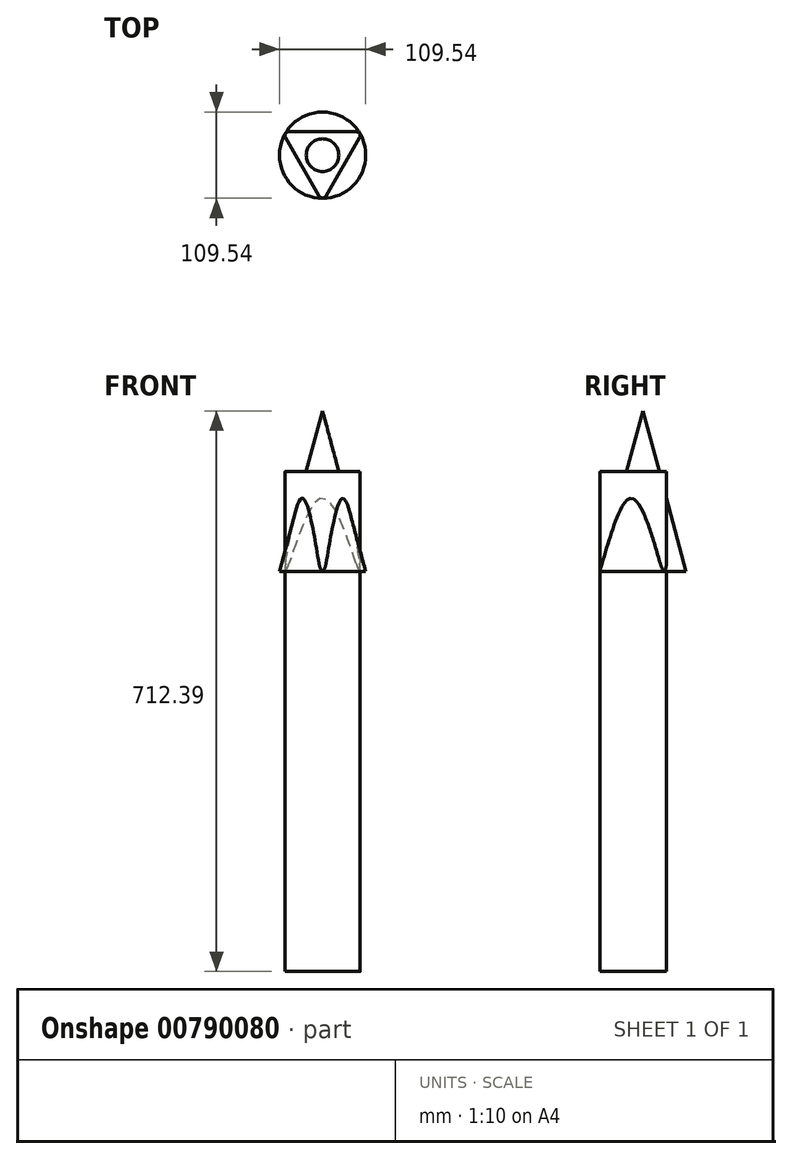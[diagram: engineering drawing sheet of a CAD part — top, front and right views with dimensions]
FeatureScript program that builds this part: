
annotation { "Feature Type Name" : "Feature", "Feature Type Description" : "" }
export const myFeature = defineFeature(function(context is Context, id is Id, definition is map)
    precondition{}
    {
        {
            var Q0;
            Q0=qCreatedBy(makeId("Top.planeOp"),FACE);
            var sketch = newSketch(context, id + "F0", { "sketchPlane" : qUnion([Q0])});
            skCircle(sketch, "E0.cCircle", {"center": v(0, 0) * mm, "radius": 29.75 * mm, "construction": true});
            skLineSegment(sketch, "E0.0", {"start": v(47.14, 22.1) * mm, "end": v(4.38, -51.88) * mm});
            skLineSegment(sketch, "E0.1", {"start": v(-4.42, -51.87) * mm, "end": v(-47.12, 22.15) * mm});
            skLineSegment(sketch, "E0.2", {"start": v(-42.71, 29.77) * mm, "end": v(42.74, 29.73) * mm});
            skPoint(sketch, "E0.0.midPoint", {"position": v(25.76, -14.89) * mm});
            skPoint(sketch, "E1.visualSharp", {"position": v(-51.51, 29.77) * mm});
            skArc(sketch, "E1.filletArc", {"start": v(-42.71, 29.77) * mm, "mid": v(-47.11, 27.23) * mm, "end": v(-47.12, 22.15) * mm});
            skPoint(sketch, "E2.visualSharp", {"position": v(51.54, 29.73) * mm});
            skArc(sketch, "E2.filletArc", {"start": v(47.14, 22.1) * mm, "mid": v(47.14, 27.19) * mm, "end": v(42.74, 29.73) * mm});
            skPoint(sketch, "E3.visualSharp", {"position": v(-0.03, -59.5) * mm});
            skArc(sketch, "E3.filletArc", {"start": v(-4.42, -51.87) * mm, "mid": v(-0.02, -54.42) * mm, "end": v(4.38, -51.88) * mm});
            skSolve(sketch);
        }
        {
            var Q0;
            Q0 = qSketchRegion(id + "F0", true);
            extrude(context, id + "F1", {"entities" : qUnion([Q0]), "depth" : 635 * mm, "offsetDistance" : 25.4 * mm});
        }
        {
            var Q0;
            Q0=qCreatedBy(makeId("Top.planeOp"),FACE);
            cPlane(context, id + "F2", {"entities" : qUnion([Q0]), "cplaneType" : CPlaneType.OFFSET, "offset" : 508 * mm, "width" : 152.4 * mm, "height" : 152.4 * mm});
        }
        {
            var Q0;
            Q0=qCreatedBy(id+"F2.planeOp",FACE);
            var sketch = newSketch(context, id + "F3", { "sketchPlane" : qUnion([Q0])});
            skCircle(sketch, "E4", {"center": v(0, 0) * mm, "radius": 54.77 * mm});
            skSolve(sketch);
        }
        {
            var Q0;
            Q0=makeQuery(id+"F3.imprint","IMPRINT",FACE,{"disambiguationData":[TD([[makeQuery(id+"F3.imprint","IMPRINT",EDGE,{"derivedFrom":sQuery(id+"F3.wireOp",EDGE,"E4")}),1.0]])]});
            extrude(context, id + "F4", {"entities" : qUnion([Q0]), "operationType" : NewBodyOperationType.ADD, "depth" : 508 * mm, "offsetDistance" : 25.4 * mm, "hasDraft" : true, "draftAngle" : 15 * degree, "draftPullDirection" : true});
        }
    });
